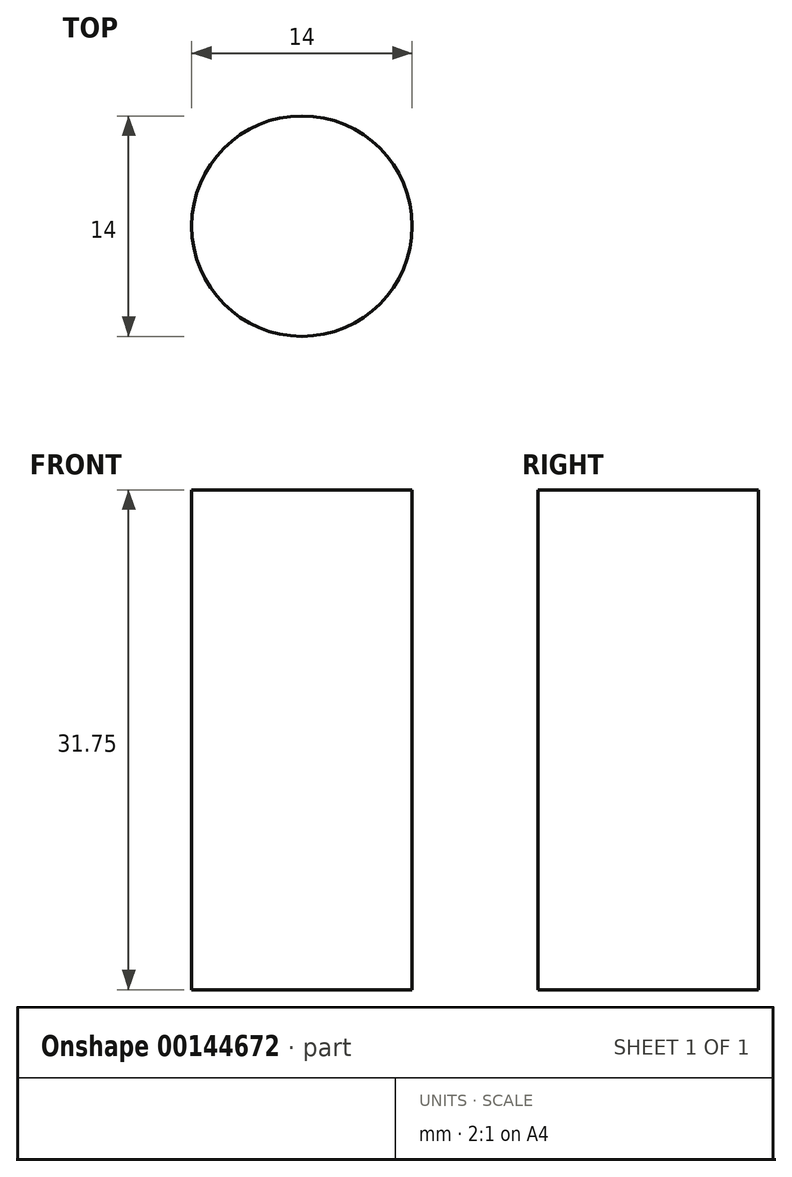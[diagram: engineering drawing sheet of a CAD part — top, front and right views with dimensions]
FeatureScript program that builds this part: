
annotation { "Feature Type Name" : "Feature", "Feature Type Description" : "" }
export const myFeature = defineFeature(function(context is Context, id is Id, definition is map)
    precondition{}
    {
        {
            var Q0;
            Q0=qCreatedBy(makeId("Top.planeOp"),FACE);
            var sketch = newSketch(context, id + "F0", { "sketchPlane" : qUnion([Q0])});
            skCircle(sketch, "E0", {"center": v(0, 0) * mm, "radius": 7 * mm});
            skSolve(sketch);
        }
        {
            var Q0;
            Q0=makeQuery(id+"F0.imprint","IMPRINT",FACE,{"disambiguationData":[TD([[makeQuery(id+"F0.imprint","IMPRINT",EDGE,{"derivedFrom":sQuery(id+"F0.wireOp",EDGE,"E0")}),1.0]])]});
            extrude(context, id + "F1", {"entities" : qUnion([Q0]), "depth" : 31.75 * mm});
        }
    });
